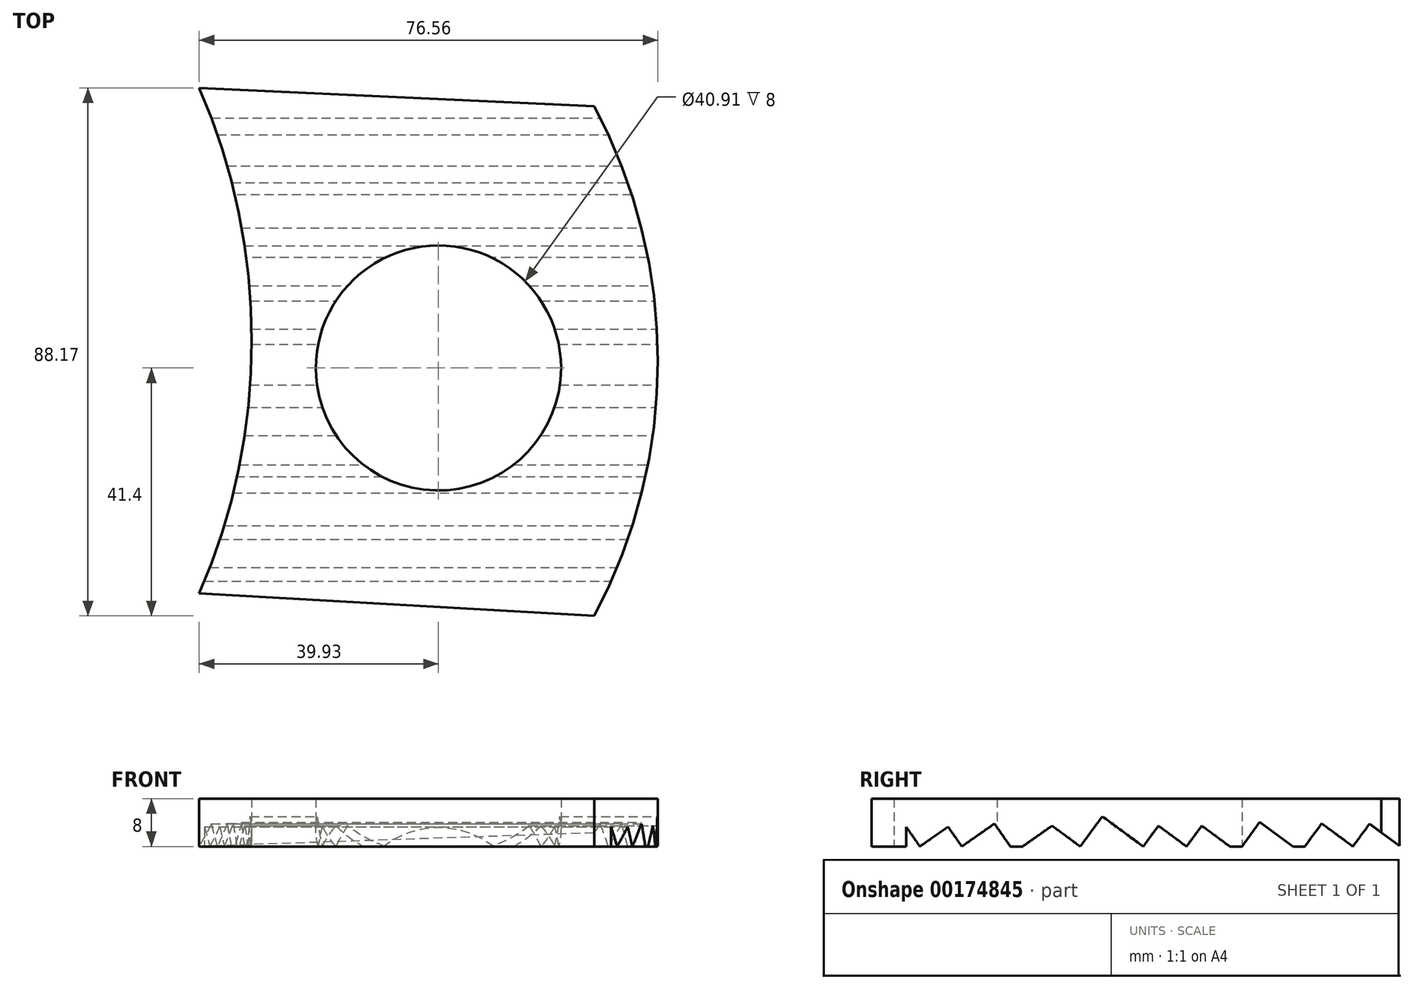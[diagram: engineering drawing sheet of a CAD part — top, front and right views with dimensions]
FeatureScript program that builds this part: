
annotation { "Feature Type Name" : "Feature", "Feature Type Description" : "" }
export const myFeature = defineFeature(function(context is Context, id is Id, definition is map)
    precondition{}
    {
        {
            var Q0;
            Q0=qCreatedBy(makeId("Top.planeOp"),FACE);
            var sketch = newSketch(context, id + "F0", { "sketchPlane" : qUnion([Q0])});
            skCircle(sketch, "E0", {"center": v(0, 0) * mm, "radius": 20.46 * mm});
            skLineSegment(sketch, "E1", {"start": v(-39.93, 46.77) * mm, "end": v(26.01, 43.71) * mm});
            skArc(sketch, "E2", {"start": v(-39.93, -37.66) * mm, "mid": v(-31.17, 4.55) * mm, "end": v(-39.93, 46.77) * mm});
            skArc(sketch, "E3", {"start": v(26.01, -41.4) * mm, "mid": v(36.63, 1.16) * mm, "end": v(26.01, 43.71) * mm});
            skLineSegment(sketch, "E4", {"start": v(-39.93, -37.66) * mm, "end": v(26.01, -41.4) * mm});
            skSolve(sketch);
        }
        {
            var Q0;
            Q0 = qSketchRegion(id + "F0", true);
            extrude(context, id + "F1", {"entities" : qUnion([Q0]), "depth" : 8 * mm});
        }
        {
            var Q0;
            Q0=qCreatedBy(makeId("Right.planeOp"),FACE);
            var sketch = newSketch(context, id + "F2", { "sketchPlane" : qUnion([Q0])});
            skLineSegment(sketch, "E5", {"start": v(46.89, 0) * mm, "end": v(41.74, 3.78) * mm});
            skLineSegment(sketch, "E6", {"start": v(41.74, 3.78) * mm, "end": v(38.96, 0) * mm});
            skLineSegment(sketch, "E7", {"start": v(38.96, 0) * mm, "end": v(33.76, 3.83) * mm});
            skLineSegment(sketch, "E8", {"start": v(33.76, 3.83) * mm, "end": v(30.24, -0.95) * mm});
            skLineSegment(sketch, "E9", {"start": v(30.24, -0.95) * mm, "end": v(23.42, 4.06) * mm});
            skLineSegment(sketch, "E10", {"start": v(23.42, 4.06) * mm, "end": v(19.73, -0.95) * mm});
            skLineSegment(sketch, "E11", {"start": v(19.73, -0.95) * mm, "end": v(13.74, 3.45) * mm});
            skLineSegment(sketch, "E12", {"start": v(13.74, 3.45) * mm, "end": v(11.2, 0) * mm});
            skLineSegment(sketch, "E13", {"start": v(11.2, 0) * mm, "end": v(6.5, 3.45) * mm});
            skLineSegment(sketch, "E14", {"start": v(6.5, 3.45) * mm, "end": v(3.96, 0) * mm});
            skLineSegment(sketch, "E15", {"start": v(3.96, 0) * mm, "end": v(-2.86, 5.02) * mm});
            skLineSegment(sketch, "E16", {"start": v(-2.86, 5.02) * mm, "end": v(-6.55, 0) * mm});
            skLineSegment(sketch, "E17", {"start": v(-6.55, 0) * mm, "end": v(-11.25, 3.45) * mm});
            skLineSegment(sketch, "E18", {"start": v(-11.25, 3.45) * mm, "end": v(-17.54, -0.95) * mm});
            skLineSegment(sketch, "E19", {"start": v(-17.54, -0.95) * mm, "end": v(-20.88, 3.8) * mm});
            skLineSegment(sketch, "E20", {"start": v(-20.88, 3.8) * mm, "end": v(-26.32, 0) * mm});
            skLineSegment(sketch, "E21", {"start": v(-26.32, 0) * mm, "end": v(-28.62, 3.29) * mm});
            skLineSegment(sketch, "E22", {"start": v(-28.62, 3.29) * mm, "end": v(-33.32, 0) * mm});
            skLineSegment(sketch, "E23", {"start": v(-33.32, 0) * mm, "end": v(-35.62, 3.29) * mm});
            skLineSegment(sketch, "E24", {"start": v(-35.62, 3.29) * mm, "end": v(-35.62, 0) * mm});
            skLineSegment(sketch, "E25", {"start": v(46.89, 0) * mm, "end": v(46.89, -9.83) * mm});
            skLineSegment(sketch, "E26", {"start": v(46.89, -9.83) * mm, "end": v(-36.6, -9.83) * mm});
            skLineSegment(sketch, "E27", {"start": v(-36.6, -9.83) * mm, "end": v(-35.62, 0) * mm});
            skSolve(sketch);
        }
        {
            var Q0;
            Q0 = qSketchRegion(id + "F2", true);
            extrude(context, id + "F3", {"entities" : qUnion([Q0]), "operationType" : NewBodyOperationType.REMOVE, "endBound" : BoundingType.THROUGH_ALL, "oppositeDirection" : true, "depth" : 25.4 * mm, "hasSecondDirection" : true, "secondDirectionBound" : SecondDirectionBoundingType.THROUGH_ALL, "secondDirectionOppositeDirection" : false, "secondDirectionDepth" : 25.4 * mm});
        }
    });
